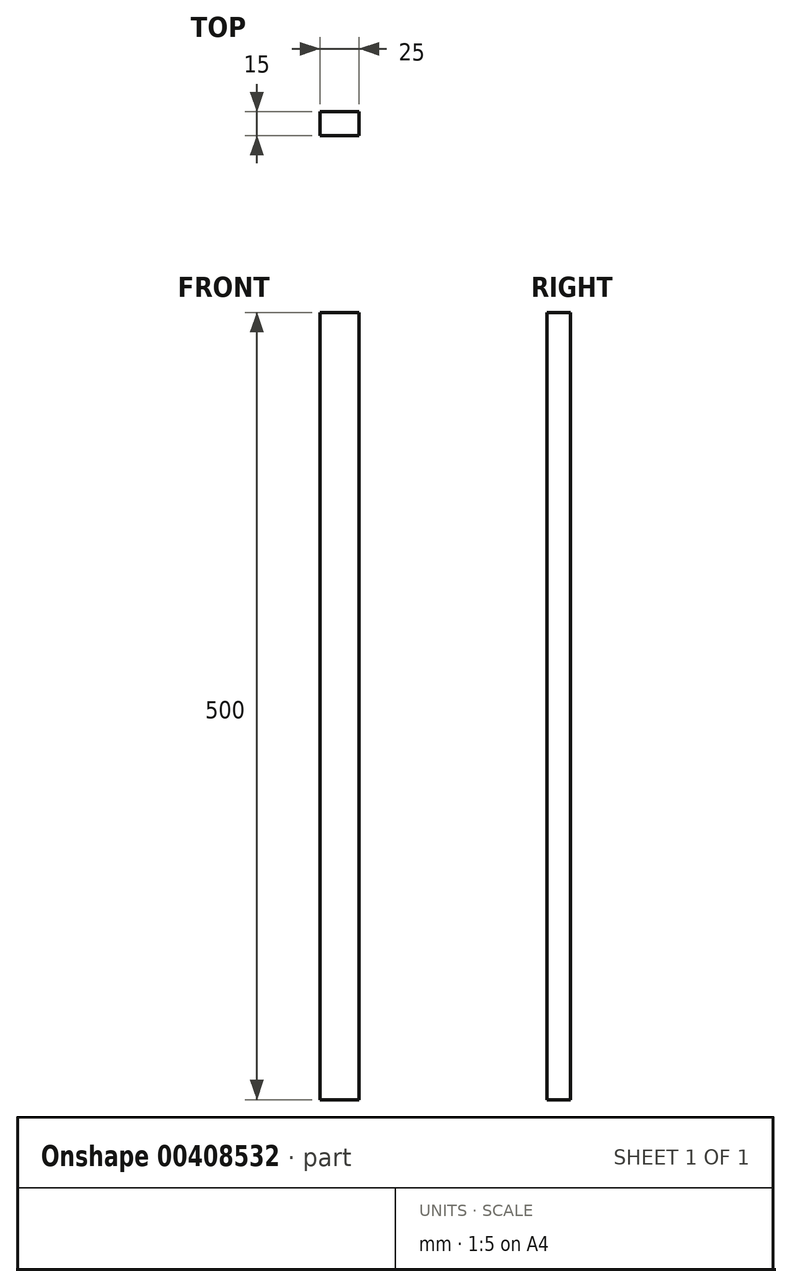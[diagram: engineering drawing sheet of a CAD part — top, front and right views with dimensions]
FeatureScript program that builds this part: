
annotation { "Feature Type Name" : "Feature", "Feature Type Description" : "" }
export const myFeature = defineFeature(function(context is Context, id is Id, definition is map)
    precondition{}
    {
        {
            var Q0;
            Q0=qCreatedBy(makeId("Top.planeOp"),FACE);
            var sketch = newSketch(context, id + "F0", { "sketchPlane" : qUnion([Q0])});
            skLineSegment(sketch, "E0.bottom", {"start": v(12.5, 7.5) * mm, "end": v(-12.5, 7.5) * mm});
            skLineSegment(sketch, "E0.top", {"start": v(12.5, -7.5) * mm, "end": v(-12.5, -7.5) * mm});
            skLineSegment(sketch, "E0.left", {"start": v(12.5, 7.5) * mm, "end": v(12.5, -7.5) * mm});
            skLineSegment(sketch, "E0.right", {"start": v(-12.5, 7.5) * mm, "end": v(-12.5, -7.5) * mm});
            skPoint(sketch, "E0.middle", {"position": v(0, 0) * mm});
            skSolve(sketch);
        }
        {
            var Q0;
            Q0 = qSketchRegion(id + "F0", true);
            extrude(context, id + "F1", {"entities" : qUnion([Q0]), "depth" : 500 * mm});
        }
    });
